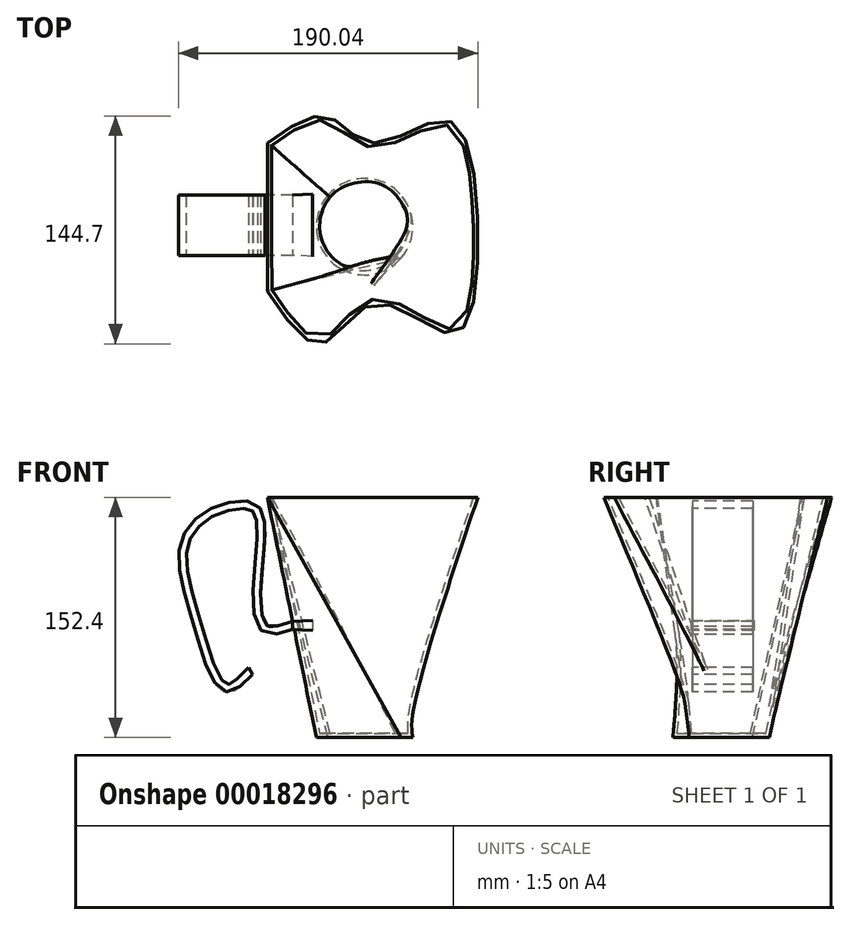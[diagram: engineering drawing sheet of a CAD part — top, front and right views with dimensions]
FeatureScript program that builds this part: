
annotation { "Feature Type Name" : "Feature", "Feature Type Description" : "" }
export const myFeature = defineFeature(function(context is Context, id is Id, definition is map)
    precondition{}
    {
        {
            var Q0;
            Q0=qCreatedBy(makeId("Top.planeOp"),FACE);
            var sketch = newSketch(context, id + "F0", { "sketchPlane" : qUnion([Q0])});
            skCircle(sketch, "E0", {"center": v(0, 0) * mm, "radius": 30.65 * mm});
            skSolve(sketch);
        }
        {
            var Q0;
            Q0=qCreatedBy(makeId("Top.planeOp"),FACE);
            cPlane(context, id + "F1", {"entities" : qUnion([Q0]), "cplaneType" : CPlaneType.OFFSET, "offset" : 152.4 * mm, "width" : 152.4 * mm, "height" : 152.4 * mm});
        }
        {
            var Q0;
            Q0=qCreatedBy(id+"F1.planeOp",FACE);
            var sketch = newSketch(context, id + "F2", { "sketchPlane" : qUnion([Q0])});
            skLineSegment(sketch, "E1", {"start": v(-61.76, 52.99) * mm, "end": v(-61.76, -41.1) * mm});
            skFitSpline(sketch, "E2", {"points": [v(-61.76, 52.99) * mm, v(-23.45, 69.64) * mm, v(5.7, 52.99) * mm, v(52.33, 67.42) * mm, v(71.76, 0) * mm, v(56.5, -67.76) * mm, v(7.08, -48.46) * mm, v(-26.5, -74.14) * mm, v(-61.76, -41.1) * mm], "startDerivative": vector(360, 260.14) * mm, "endDerivative": vector(-296.62, 440.88) * mm});
            skSolve(sketch);
        }
        {
            var Q0;
            Q0=makeQuery(id+"F0.imprint","IMPRINT",FACE,{"disambiguationData":[TD([[makeQuery(id+"F0.imprint","IMPRINT",EDGE,{"derivedFrom":sQuery(id+"F0.wireOp",EDGE,"E0")}),1.0]])]});
            var Q1;
            Q1=makeQuery(id+"F2.imprint","IMPRINT",FACE,{"disambiguationData":[TD([[makeQuery(id+"F2.imprint","IMPRINT",EDGE,{"derivedFrom":sQuery(id+"F2.wireOp",EDGE,"E1")}),1.0]])]});
            loft(context, id + "F3", {"sheetProfilesArray" : [{ "sheetProfileEntities" : qUnion([Q0]) }, { "sheetProfileEntities" : qUnion([Q1]) }]});
        }
        {
            var Q0;
            Q0=makeQuery(id+"F3.opLoft","CAP_FACE",FACE,{"disambiguationData":[OSD([makeQuery(id+"F2.imprint","IMPRINT",FACE,{"disambiguationData":[TD([[makeQuery(id+"F2.imprint","IMPRINT",EDGE,{"derivedFrom":sQuery(id+"F2.wireOp",EDGE,"E1")}),1.0]])]})])],"isStart":true});
            shell(context, id + "F4", {"entities" : qUnion([Q0]), "thickness" : 2.54 * mm});
        }
        {
            var Q0;
            Q0=qCreatedBy(makeId("Right.planeOp"),FACE);
            cPlane(context, id + "F5", {"entities" : qUnion([Q0]), "cplaneType" : CPlaneType.OFFSET, "offset" : 45.72 * mm, "oppositeDirection" : true, "width" : 152.4 * mm, "height" : 152.4 * mm});
        }
        {
            var Q0;
            Q0=qCreatedBy(id+"F5.planeOp",FACE);
            var sketch = newSketch(context, id + "F6", { "sketchPlane" : qUnion([Q0])});
            skLineSegment(sketch, "E3.bottom", {"start": v(20.13, 73.6) * mm, "end": v(-18.17, 73.6) * mm});
            skLineSegment(sketch, "E3.top", {"start": v(20.13, 68.46) * mm, "end": v(-18.17, 68.46) * mm});
            skLineSegment(sketch, "E3.left", {"start": v(20.13, 73.6) * mm, "end": v(20.13, 68.46) * mm});
            skLineSegment(sketch, "E3.right", {"start": v(-18.17, 73.6) * mm, "end": v(-18.17, 68.46) * mm});
            skSolve(sketch);
        }
        {
            var Q0;
            Q0=qCreatedBy(makeId("Front.planeOp"),FACE);
            var sketch = newSketch(context, id + "F7", { "sketchPlane" : qUnion([Q0])});
            skFitSpline(sketch, "E4", {"points": [v(-45.75, 71.23) * mm, v(-64.77, 70.68) * mm, v(-65.74, 125.1) * mm, v(-70.88, 146.63) * mm, v(-97.82, 142.6) * mm, v(-115.31, 120.25) * mm, v(-106.7, 72.76) * mm, v(-88.51, 31.38) * mm, v(-72.4, 42.07) * mm], "startDerivative": vector(-235.45, -80.5) * mm, "endDerivative": vector(173.46, 189.42) * mm});
            skSolve(sketch);
        }
        {
            var Q0;
            Q0=makeQuery(id+"F6.imprint","IMPRINT",FACE,{"disambiguationData":[TD([[makeQuery(id+"F6.imprint","IMPRINT",EDGE,{"derivedFrom":sQuery(id+"F6.wireOp",EDGE,"E3.bottom")}),1.0]])]});
            var Q1;
            Q1=sQuery(id+"F7.wireOp",EDGE,"E4");
            sweep(context, id + "F8", {"profiles" : qUnion([Q0]), "path" : qUnion([Q1])});
        }
        {
            var Q0;
            Q0=makeQuery(id+"F8.opSweep","CAP_FACE",FACE,{"disambiguationData":[OSD([sQuery(id+"F6.wireOp",EDGE,"E3.bottom"),sQuery(id+"F6.wireOp",EDGE,"E3.top"),sQuery(id+"F6.wireOp",EDGE,"E3.left"),sQuery(id+"F6.wireOp",EDGE,"E3.right"),sQuery(id+"F7.wireOp",VERTEX,"E4.start")])],"isStart":true});
            extrude(context, id + "F9", {"entities" : qUnion([Q0]), "depth" : 12.7 * mm, "hasDraft" : true, "draftAngle" : 3 * degree});
        }
    });
